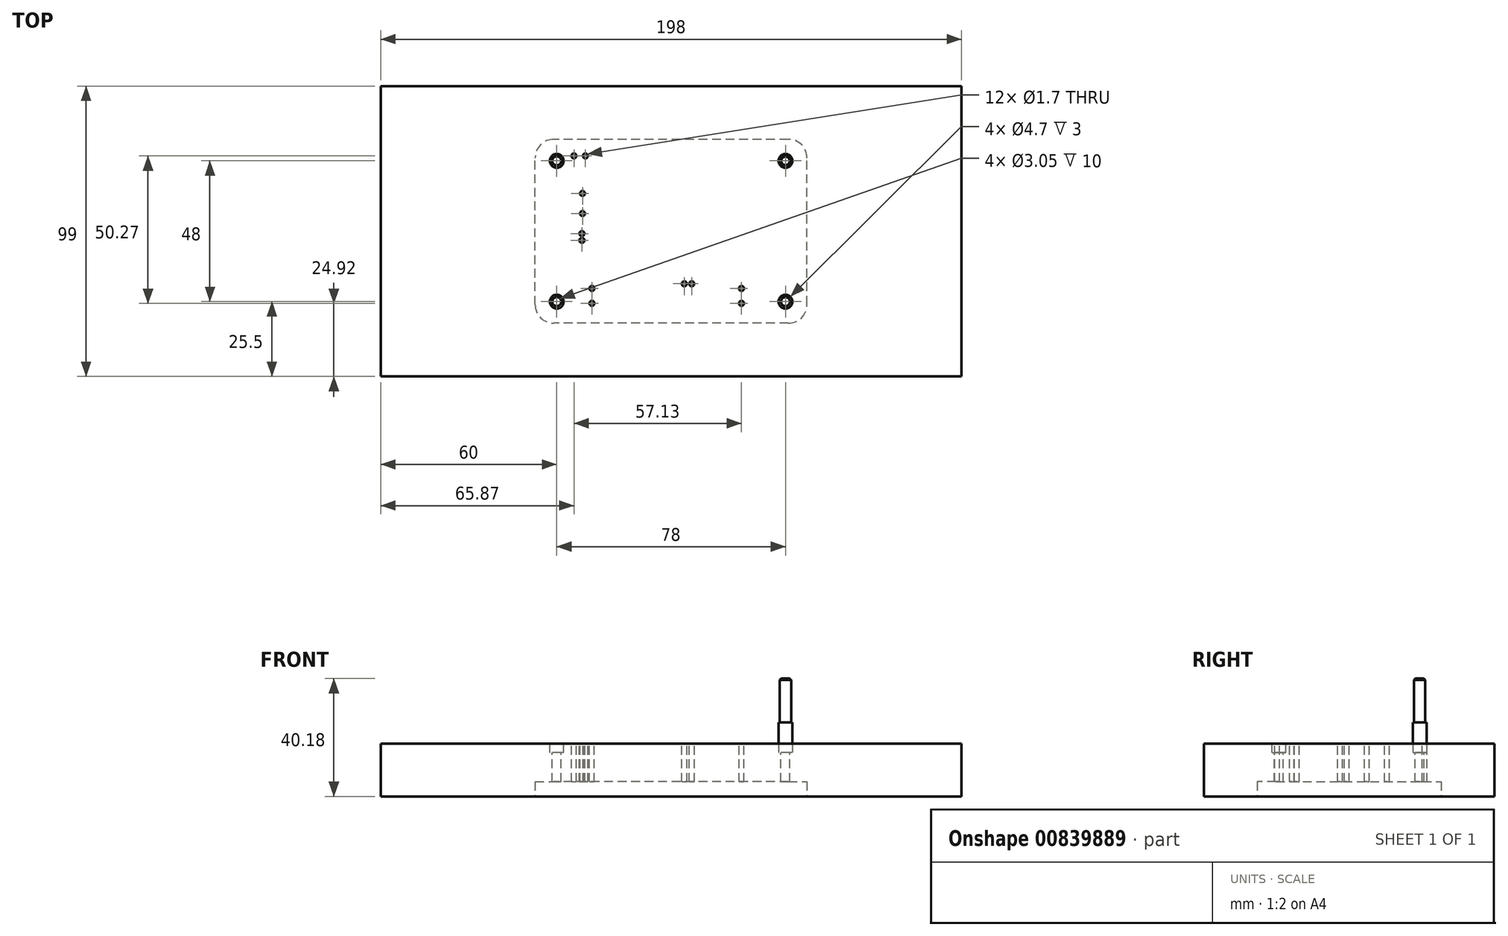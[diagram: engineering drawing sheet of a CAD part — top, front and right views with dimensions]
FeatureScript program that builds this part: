
annotation { "Feature Type Name" : "Feature", "Feature Type Description" : "" }
export const myFeature = defineFeature(function(context is Context, id is Id, definition is map)
    precondition{}
    {
        {
            var Q0;
            Q0=qCreatedBy(makeId("Top.planeOp"),FACE);
            var sketch = newSketch(context, id + "F0", { "sketchPlane" : qUnion([Q0])});
            skLineSegment(sketch, "E0.bottom", {"start": v(-99, -49.5) * mm, "end": v(99, -49.5) * mm});
            skLineSegment(sketch, "E0.top", {"start": v(-99, 49.5) * mm, "end": v(99, 49.5) * mm});
            skLineSegment(sketch, "E0.left", {"start": v(-99, -49.5) * mm, "end": v(-99, 49.5) * mm});
            skLineSegment(sketch, "E0.right", {"start": v(99, -49.5) * mm, "end": v(99, 49.5) * mm});
            skPoint(sketch, "E0.middle", {"position": v(0, 0) * mm});
            skLineSegment(sketch, "E1.bottom", {"start": v(-40, -25) * mm, "end": v(40, -25) * mm, "construction": true});
            skLineSegment(sketch, "E1.top", {"start": v(-40, 25) * mm, "end": v(40, 25) * mm, "construction": true});
            skLineSegment(sketch, "E1.left", {"start": v(-40, -25) * mm, "end": v(-40, 25) * mm, "construction": true});
            skLineSegment(sketch, "E1.right", {"start": v(40, -25) * mm, "end": v(40, 25) * mm, "construction": true});
            skSolve(sketch);
        }
        {
            var Q0;
            Q0 = qSketchRegion(id + "F0", true);
            extrude(context, id + "F1", {"entities" : qUnion([Q0]), "oppositeDirection" : true, "depth" : 18 * mm, "offsetDistance" : 25 * mm});
        }
        {
            var Q0;
            Q0=makeQuery(id+"F1.opExtrude","CAP_FACE",FACE,{"disambiguationData":[OSD([sQuery(id+"F0.wireOp",EDGE,"E0.bottom"),sQuery(id+"F0.wireOp",EDGE,"E0.top"),sQuery(id+"F0.wireOp",EDGE,"E0.left"),sQuery(id+"F0.wireOp",EDGE,"E0.right")])],"isStart":false});
            var sketch = newSketch(context, id + "F2", { "sketchPlane" : qUnion([Q0])});
            skLineSegment(sketch, "E2.bottom", {"start": v(40, 31.35) * mm, "end": v(-40, 31.35) * mm});
            skLineSegment(sketch, "E2.top", {"start": v(40, -31.35) * mm, "end": v(-40, -31.35) * mm});
            skLineSegment(sketch, "E2.left", {"start": v(46.35, 25) * mm, "end": v(46.35, -25) * mm});
            skLineSegment(sketch, "E2.right", {"start": v(-46.35, 25) * mm, "end": v(-46.35, -25) * mm});
            skPoint(sketch, "E2.middle", {"position": v(0, 0) * mm});
            skPoint(sketch, "E3.visualSharp", {"position": v(46.35, -31.35) * mm});
            skArc(sketch, "E3.filletArc", {"start": v(40, -31.35) * mm, "mid": v(44.5, -29.5) * mm, "end": v(46.35, -25) * mm});
            skPoint(sketch, "E4.visualSharp", {"position": v(-46.35, -31.35) * mm});
            skArc(sketch, "E4.filletArc", {"start": v(-46.35, -25) * mm, "mid": v(-44.5, -29.5) * mm, "end": v(-40, -31.35) * mm});
            skPoint(sketch, "E5.visualSharp", {"position": v(-46.35, 31.35) * mm});
            skArc(sketch, "E5.filletArc", {"start": v(-40, 31.35) * mm, "mid": v(-44.5, 29.5) * mm, "end": v(-46.35, 25) * mm});
            skPoint(sketch, "E6.visualSharp", {"position": v(46.35, 31.35) * mm});
            skArc(sketch, "E6.filletArc", {"start": v(46.35, 25) * mm, "mid": v(44.5, 29.5) * mm, "end": v(40, 31.35) * mm});
            skSolve(sketch);
        }
        {
            var Q0;
            Q0 = qSketchRegion(id + "F2", true);
            extrude(context, id + "F3", {"entities" : qUnion([Q0]), "operationType" : NewBodyOperationType.REMOVE, "oppositeDirection" : true, "depth" : 5 * mm, "offsetDistance" : 25 * mm});
        }
        {
            var Q0;
            Q0=makeQuery(id+"F0.imprint","IMPRINT",FACE,{"disambiguationData":[TD([[makeQuery(id+"F0.imprint","IMPRINT",EDGE,{"derivedFrom":sQuery(id+"F0.wireOp",EDGE,"E0.bottom")}),1.0]])]});
            var sketch = newSketch(context, id + "F4", { "sketchPlane" : qUnion([Q0])});
            skCircle(sketch, "E7", {"center": v(-39, -24) * mm, "radius": 2.35 * mm});
            skCircle(sketch, "E8", {"center": v(39, -24) * mm, "radius": 2.35 * mm});
            skCircle(sketch, "E9", {"center": v(39, 24) * mm, "radius": 2.35 * mm});
            skCircle(sketch, "E10", {"center": v(-39, 24) * mm, "radius": 2.35 * mm});
            skSolve(sketch);
        }
        {
            var Q0;
            Q0 = qSketchRegion(id + "F4", true);
            extrude(context, id + "F5", {"entities" : qUnion([Q0]), "operationType" : NewBodyOperationType.REMOVE, "oppositeDirection" : true, "depth" : 3 * mm, "offsetDistance" : 25 * mm});
        }
        {
            var Q0;
            Q0=makeQuery(id+"F0.imprint","IMPRINT",FACE,{"disambiguationData":[TD([[makeQuery(id+"F0.imprint","IMPRINT",EDGE,{"derivedFrom":sQuery(id+"F0.wireOp",EDGE,"E0.bottom")}),1.0]])]});
            var sketch = newSketch(context, id + "F6", { "sketchPlane" : qUnion([Q0])});
            skCircle(sketch, "E11", {"center": v(-39, 24) * mm, "radius": 1.52 * mm});
            skCircle(sketch, "E12", {"center": v(-39, -24) * mm, "radius": 1.52 * mm});
            skCircle(sketch, "E13", {"center": v(39, -24) * mm, "radius": 1.52 * mm});
            skCircle(sketch, "E14", {"center": v(39, 24) * mm, "radius": 1.52 * mm});
            skSolve(sketch);
        }
        {
            var Q0;
            Q0=makeQuery(id+"F0.imprint","IMPRINT",FACE,{"disambiguationData":[TD([[makeQuery(id+"F0.imprint","IMPRINT",EDGE,{"derivedFrom":sQuery(id+"F0.wireOp",EDGE,"E0.bottom")}),1.0]])]});
            var sketch = newSketch(context, id + "F7", { "sketchPlane" : qUnion([Q0])});
            skCircle(sketch, "E15", {"center": v(4.5, -17.9) * mm, "radius": 0.85 * mm});
            skCircle(sketch, "E16", {"center": v(7.04, -17.9) * mm, "radius": 0.85 * mm});
            skCircle(sketch, "E17", {"center": v(24, -19.5) * mm, "radius": 0.85 * mm});
            skCircle(sketch, "E18", {"center": v(24, -24.58) * mm, "radius": 0.85 * mm});
            skCircle(sketch, "E19", {"center": v(-27, -19.5) * mm, "radius": 0.85 * mm});
            skCircle(sketch, "E20", {"center": v(-27, -24.58) * mm, "radius": 0.85 * mm});
            skCircle(sketch, "E21", {"center": v(-33.13, 25.69) * mm, "radius": 0.85 * mm});
            skCircle(sketch, "E22", {"center": v(-30.2, 12.9) * mm, "radius": 0.85 * mm});
            skCircle(sketch, "E23", {"center": v(-30.2, 6.04) * mm, "radius": 0.85 * mm});
            skCircle(sketch, "E24", {"center": v(-30.4, -0.8) * mm, "radius": 0.85 * mm});
            skCircle(sketch, "E25", {"center": v(-30.4, -3.1) * mm, "radius": 0.85 * mm});
            skCircle(sketch, "E26", {"center": v(-29.23, 25.69) * mm, "radius": 0.85 * mm});
            skSolve(sketch);
        }
        {
            var Q0;
            Q0 = qSketchRegion(id + "F7", true);
            extrude(context, id + "F8", {"entities" : qUnion([Q0]), "operationType" : NewBodyOperationType.REMOVE, "endBound" : BoundingType.THROUGH_ALL, "oppositeDirection" : true, "depth" : 25 * mm, "offsetDistance" : 25 * mm});
        }
        {
            var Q0;
            Q0 = qSketchRegion(id + "F6", true);
            extrude(context, id + "F9", {"entities" : qUnion([Q0]), "operationType" : NewBodyOperationType.REMOVE, "endBound" : BoundingType.THROUGH_ALL, "oppositeDirection" : true, "depth" : 25 * mm, "offsetDistance" : 25 * mm});
        }
        {
            var Q0;
            Q0=qCreatedBy(makeId("Top.planeOp"),FACE);
            cPlane(context, id + "F10", {"entities" : qUnion([Q0]), "cplaneType" : CPlaneType.OFFSET, "offset" : 3 * mm, "oppositeDirection" : true, "width" : 150 * mm, "height" : 150 * mm});
        }
        {
            var Q0;
            Q0=qCreatedBy(id+"F10.planeOp",FACE);
            var sketch = newSketch(context, id + "F11", { "sketchPlane" : qUnion([Q0])});
            skCircle(sketch, "E27", {"center": v(39, 24) * mm, "radius": 2.35 * mm});
            skSolve(sketch);
        }
        {
            var Q0;
            Q0 = qSketchRegion(id + "F11", true);
            extrude(context, id + "F12", {"entities" : qUnion([Q0]), "depth" : 10.18 * mm, "offsetDistance" : 25 * mm});
        }
        {
            var Q0;
            Q0=makeQuery(id+"F12.opExtrude","CAP_FACE",FACE,{"disambiguationData":[OSD([sQuery(id+"F11.wireOp",EDGE,"E27")])],"isStart":false});
            var sketch = newSketch(context, id + "F13", { "sketchPlane" : qUnion([Q0])});
            skCircle(sketch, "E28", {"center": v(39, 24) * mm, "radius": 1.92 * mm});
            skSolve(sketch);
        }
        {
            var Q0;
            Q0 = qSketchRegion(id + "F13", true);
            extrude(context, id + "F14", {"entities" : qUnion([Q0]), "operationType" : NewBodyOperationType.ADD, "depth" : 15 * mm, "offsetDistance" : 25 * mm});
        }
        {
            var Q0;
            Q0=makeQuery(id+"F14.opExtrude","CAP_EDGE",EDGE,{"disambiguationData":[OSD([sQuery(id+"F13.wireOp",EDGE,"E28")])],"isStart":false});
            chamfer(context, id + "F15", {"entities" : qUnion([Q0]), "width" : .5 * mm, "tangentPropagation" : true});
        }
    });
